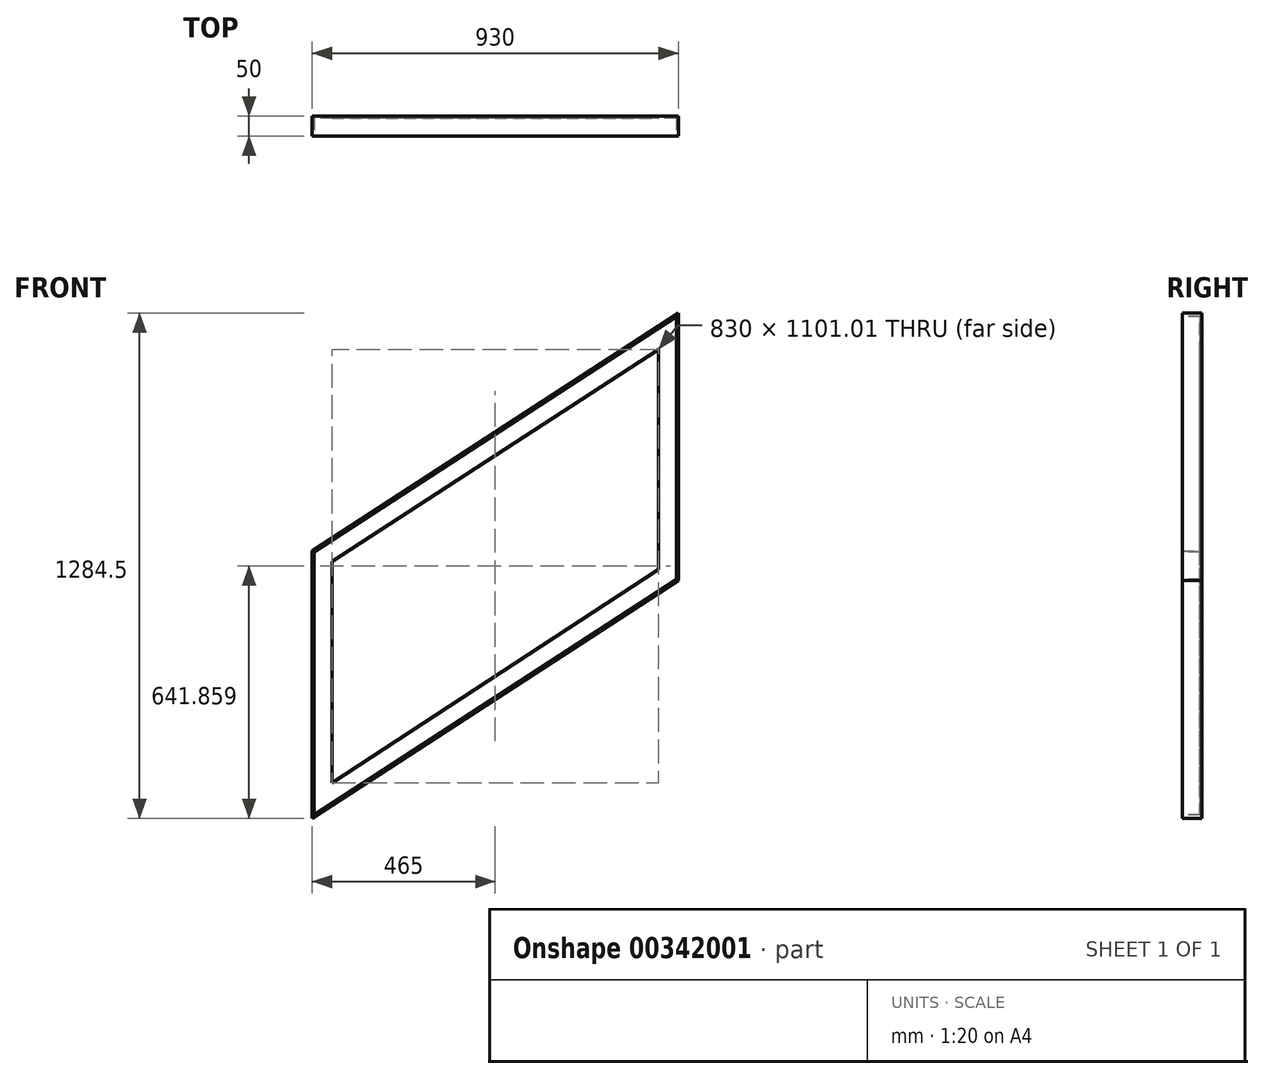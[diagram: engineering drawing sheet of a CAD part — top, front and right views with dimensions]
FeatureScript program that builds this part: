
annotation { "Feature Type Name" : "Feature", "Feature Type Description" : "" }
export const myFeature = defineFeature(function(context is Context, id is Id, definition is map)
    precondition{}
    {
        {
            var Q0;
            Q0=qCreatedBy(makeId("Front.planeOp"),FACE);
            var sketch = newSketch(context, id + "F0", { "sketchPlane" : qUnion([Q0])});
            skLineSegment(sketch, "E0", {"start": v(35, 122.75) * mm, "end": v(35, 802.75) * mm});
            skLineSegment(sketch, "E1", {"start": v(965, 727.25) * mm, "end": v(965, 1407.25) * mm});
            skLineSegment(sketch, "E2", {"start": v(965, 1407.25) * mm, "end": v(35, 802.75) * mm});
            skLineSegment(sketch, "E3", {"start": v(965, 727.25) * mm, "end": v(35, 122.75) * mm});
            skLineSegment(sketch, "E4", {"start": v(85, 214.1) * mm, "end": v(85, 775.62) * mm});
            skLineSegment(sketch, "E5", {"start": v(85, 775.62) * mm, "end": v(915, 1315.12) * mm});
            skLineSegment(sketch, "E6", {"start": v(915, 1315.12) * mm, "end": v(915, 756.37) * mm});
            skLineSegment(sketch, "E7", {"start": v(85, 214.1) * mm, "end": v(915, 756.37) * mm});
            skSolve(sketch);
        }
        {
            var Q0;
            Q0 = qSketchRegion(id + "F0", true);
            extrude(context, id + "F1", {"entities" : qUnion([Q0]), "depth" : 50 * mm});
        }
        {
            var Q0;
            Q0=makeQuery(id+"F1.opExtrude","CAP_FACE",FACE,{"disambiguationData":[OSD([sQuery(id+"F0.wireOp",EDGE,"E0"),sQuery(id+"F0.wireOp",EDGE,"E1"),sQuery(id+"F0.wireOp",EDGE,"E2"),sQuery(id+"F0.wireOp",EDGE,"E3"),sQuery(id+"F0.wireOp",EDGE,"E4"),sQuery(id+"F0.wireOp",EDGE,"E5"),sQuery(id+"F0.wireOp",EDGE,"E6"),sQuery(id+"F0.wireOp",EDGE,"E7")])],"isStart":false});
            var sketch = newSketch(context, id + "F2", { "sketchPlane" : qUnion([Q0])});
            skLineSegment(sketch, "E8", {"start": v(40, 131.96) * mm, "end": v(40, 800.04) * mm});
            skLineSegment(sketch, "E9", {"start": v(40, 800.04) * mm, "end": v(960, 1398.04) * mm});
            skLineSegment(sketch, "E10", {"start": v(960, 1398.04) * mm, "end": v(960, 729.96) * mm});
            skLineSegment(sketch, "E11", {"start": v(960, 729.96) * mm, "end": v(40, 131.96) * mm});
            skSolve(sketch);
        }
        {
            var Q0;
            Q0 = qSketchRegion(id + "F2", true);
            extrude(context, id + "F3", {"entities" : qUnion([Q0]), "operationType" : NewBodyOperationType.REMOVE, "oppositeDirection" : true, "depth" : 45 * mm});
        }
    });
